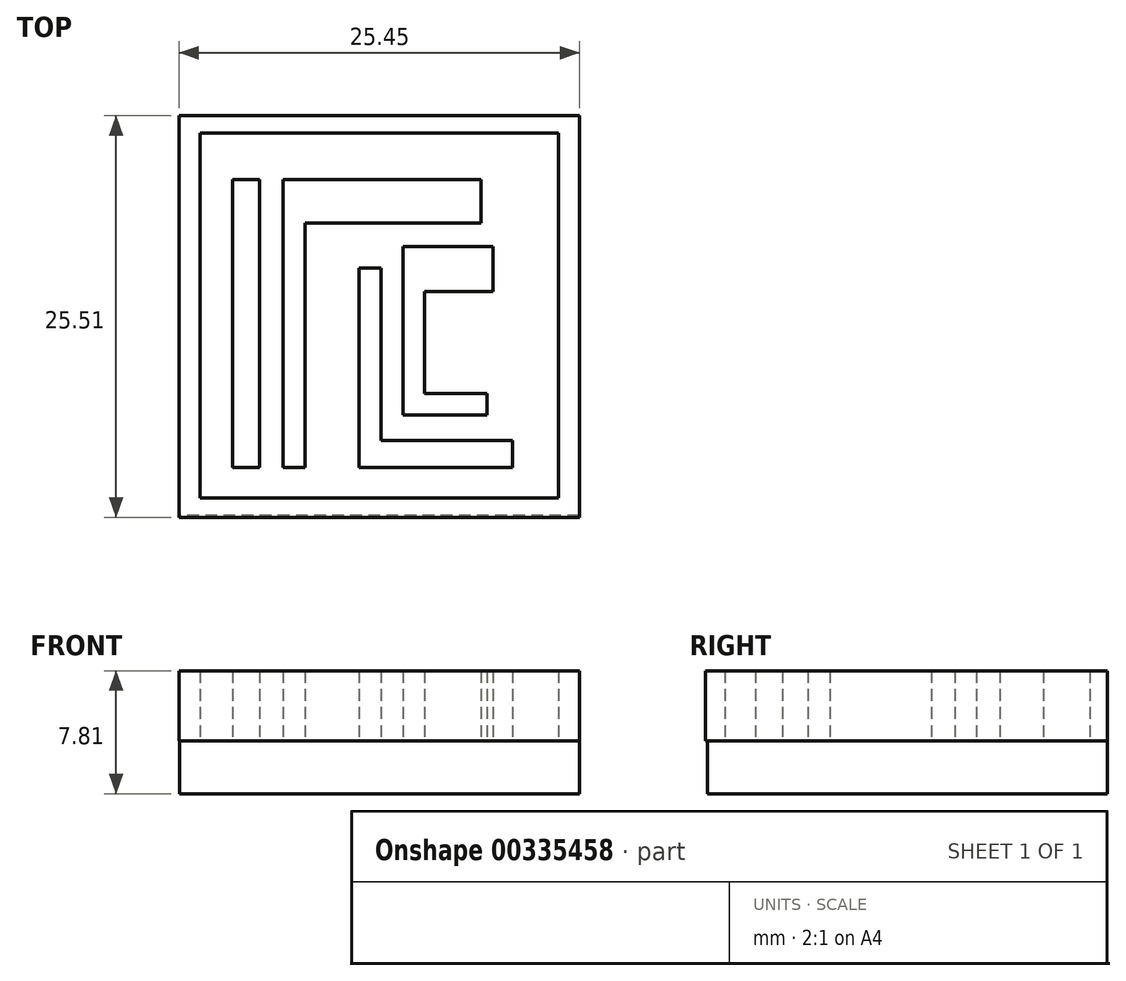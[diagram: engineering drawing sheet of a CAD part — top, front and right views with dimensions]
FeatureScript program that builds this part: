
annotation { "Feature Type Name" : "Feature", "Feature Type Description" : "" }
export const myFeature = defineFeature(function(context is Context, id is Id, definition is map)
    precondition{}
    {
        {
            var Q0;
            Q0=qCreatedBy(makeId("Front.planeOp"),FACE);
            var sketch = newSketch(context, id + "F0", { "sketchPlane" : qUnion([Q0])});
            skLineSegment(sketch, "E0", {"start": v(-11.4, 0) * mm, "end": v(14, 0) * mm});
            skLineSegment(sketch, "E1", {"start": v(14, 0) * mm, "end": v(14, -3.36) * mm});
            skLineSegment(sketch, "E2", {"start": v(14, -3.36) * mm, "end": v(-11.4, -3.36) * mm});
            skLineSegment(sketch, "E3", {"start": v(-11.4, -3.36) * mm, "end": v(-11.4, 0) * mm});
            skSolve(sketch);
        }
        {
            var Q0;
            Q0=makeQuery(id+"F0.imprint","IMPRINT",FACE,{"disambiguationData":[TD([[makeQuery(id+"F0.imprint","IMPRINT",EDGE,{"derivedFrom":sQuery(id+"F0.wireOp",EDGE,"E0")}),-1.0]])]});
            extrude(context, id + "F1", {"entities" : qUnion([Q0]), "depth" : 25.4 * mm});
        }
        {
            var Q0;
            Q0=qCreatedBy(makeId("Top.planeOp"),FACE);
            var sketch = newSketch(context, id + "F2", { "sketchPlane" : qUnion([Q0])});
            skLineSegment(sketch, "E4", {"start": v(-11.43, 0) * mm, "end": v(-11.43, -25.51) * mm});
            skLineSegment(sketch, "E5", {"start": v(-11.43, -25.51) * mm, "end": v(14.02, -25.51) * mm});
            skLineSegment(sketch, "E6", {"start": v(14.02, -25.51) * mm, "end": v(14.02, 0) * mm});
            skLineSegment(sketch, "E7", {"start": v(14.02, 0) * mm, "end": v(-11.43, 0) * mm});
            skLineSegment(sketch, "E8", {"start": v(-11.43, 0) * mm, "end": v(-10.1, -1.11) * mm});
            skLineSegment(sketch, "E9", {"start": v(-11.43, -25.51) * mm, "end": v(-10.1, -24.28) * mm});
            skLineSegment(sketch, "E10", {"start": v(-10.1, -24.28) * mm, "end": v(-10.1, -1.11) * mm});
            skLineSegment(sketch, "E11", {"start": v(14.02, 0) * mm, "end": v(12.69, -1.11) * mm});
            skLineSegment(sketch, "E12", {"start": v(12.69, -1.11) * mm, "end": v(12.69, -24.28) * mm});
            skLineSegment(sketch, "E13", {"start": v(12.69, -24.28) * mm, "end": v(14.02, -25.51) * mm});
            skLineSegment(sketch, "E14", {"start": v(12.69, -24.28) * mm, "end": v(-10.1, -24.28) * mm});
            skLineSegment(sketch, "E15", {"start": v(-10.1, -1.11) * mm, "end": v(12.69, -1.11) * mm});
            skSolve(sketch);
        }
        {
            var Q0;
            Q0=makeQuery(id+"F2.imprint","IMPRINT",FACE,{"disambiguationData":[TD([[makeQuery(id+"F2.imprint","IMPRINT",EDGE,{"derivedFrom":sQuery(id+"F2.wireOp",EDGE,"E4")}),1.0]])]});
            var Q1;
            Q1=makeQuery(id+"F2.imprint","IMPRINT",FACE,{"disambiguationData":[TD([[makeQuery(id+"F2.imprint","IMPRINT",EDGE,{"derivedFrom":sQuery(id+"F2.wireOp",EDGE,"E8")}),1.0]])]});
            var Q2;
            Q2=makeQuery(id+"F2.imprint","IMPRINT",FACE,{"disambiguationData":[TD([[makeQuery(id+"F2.imprint","IMPRINT",EDGE,{"derivedFrom":sQuery(id+"F2.wireOp",EDGE,"E6")}),1.0]])]});
            var Q3;
            Q3=makeQuery(id+"F2.imprint","IMPRINT",FACE,{"disambiguationData":[TD([[makeQuery(id+"F2.imprint","IMPRINT",EDGE,{"derivedFrom":sQuery(id+"F2.wireOp",EDGE,"E5")}),1.0]])]});
            extrude(context, id + "F3", {"entities" : qUnion([Q0, Q1, Q2, Q3]), "operationType" : NewBodyOperationType.ADD, "depth" : 4.44 * mm});
        }
        {
            var Q0;
            Q0=qCreatedBy(makeId("Top.planeOp"),FACE);
            var sketch = newSketch(context, id + "F4", { "sketchPlane" : qUnion([Q0])});
            skLineSegment(sketch, "E16", {"start": v(-8.04, -22.36) * mm, "end": v(-8.04, -4.07) * mm});
            skLineSegment(sketch, "E17", {"start": v(-8.04, -4.07) * mm, "end": v(-6.3, -4.07) * mm});
            skLineSegment(sketch, "E18", {"start": v(-6.3, -4.07) * mm, "end": v(-6.3, -22.36) * mm});
            skLineSegment(sketch, "E19", {"start": v(-6.3, -22.36) * mm, "end": v(-8.04, -22.36) * mm});
            skLineSegment(sketch, "E20", {"start": v(0, -4.07) * mm, "end": v(7.77, -4.07) * mm});
            skLineSegment(sketch, "E21", {"start": v(7.77, -4.07) * mm, "end": v(7.77, -6.8) * mm});
            skLineSegment(sketch, "E22", {"start": v(7.77, -6.8) * mm, "end": v(-3.43, -6.8) * mm});
            skLineSegment(sketch, "E23", {"start": v(-3.43, -6.8) * mm, "end": v(-3.43, -22.36) * mm});
            skLineSegment(sketch, "E24", {"start": v(-3.43, -22.36) * mm, "end": v(-4.8, -22.36) * mm});
            skLineSegment(sketch, "E25", {"start": v(-4.8, -22.36) * mm, "end": v(-4.8, -4.07) * mm});
            skLineSegment(sketch, "E26", {"start": v(-4.8, -4.07) * mm, "end": v(0, -4.07) * mm});
            skLineSegment(sketch, "E27", {"start": v(0, -9.66) * mm, "end": v(0, -22.36) * mm});
            skLineSegment(sketch, "E28", {"start": v(0, -22.36) * mm, "end": v(9.76, -22.36) * mm});
            skLineSegment(sketch, "E29", {"start": v(9.76, -22.36) * mm, "end": v(9.76, -20.62) * mm});
            skLineSegment(sketch, "E30", {"start": v(9.76, -20.62) * mm, "end": v(1.42, -20.62) * mm});
            skLineSegment(sketch, "E31", {"start": v(1.42, -20.62) * mm, "end": v(1.42, -9.66) * mm});
            skLineSegment(sketch, "E32", {"start": v(1.42, -9.66) * mm, "end": v(0, -9.66) * mm});
            skLineSegment(sketch, "E33", {"start": v(8.51, -8.3) * mm, "end": v(8.51, -11.16) * mm});
            skLineSegment(sketch, "E34", {"start": v(8.51, -11.16) * mm, "end": v(4.16, -11.16) * mm});
            skLineSegment(sketch, "E35", {"start": v(4.16, -11.16) * mm, "end": v(4.16, -17.63) * mm});
            skLineSegment(sketch, "E36", {"start": v(4.16, -17.63) * mm, "end": v(8.14, -17.63) * mm});
            skLineSegment(sketch, "E37", {"start": v(8.14, -17.63) * mm, "end": v(8.14, -19) * mm});
            skLineSegment(sketch, "E38", {"start": v(8.14, -19) * mm, "end": v(2.79, -19) * mm});
            skLineSegment(sketch, "E39", {"start": v(2.79, -19) * mm, "end": v(2.79, -8.3) * mm});
            skLineSegment(sketch, "E40", {"start": v(2.79, -8.3) * mm, "end": v(8.51, -8.3) * mm});
            skSolve(sketch);
        }
        {
            var Q0;
            Q0=makeQuery(id+"F4.imprint","IMPRINT",FACE,{"disambiguationData":[TD([[makeQuery(id+"F4.imprint","IMPRINT",EDGE,{"derivedFrom":sQuery(id+"F4.wireOp",EDGE,"E16")}),-1.0]])]});
            var Q1;
            Q1=makeQuery(id+"F4.imprint","IMPRINT",FACE,{"disambiguationData":[TD([[makeQuery(id+"F4.imprint","IMPRINT",EDGE,{"derivedFrom":sQuery(id+"F4.wireOp",EDGE,"E20")}),-1.0]])]});
            var Q2;
            Q2=makeQuery(id+"F4.imprint","IMPRINT",FACE,{"disambiguationData":[TD([[makeQuery(id+"F4.imprint","IMPRINT",EDGE,{"derivedFrom":sQuery(id+"F4.wireOp",EDGE,"E27")}),1.0]])]});
            var Q3;
            Q3=makeQuery(id+"F4.imprint","IMPRINT",FACE,{"disambiguationData":[TD([[makeQuery(id+"F4.imprint","IMPRINT",EDGE,{"derivedFrom":sQuery(id+"F4.wireOp",EDGE,"E33")}),-1.0]])]});
            extrude(context, id + "F5", {"entities" : qUnion([Q0, Q1, Q2, Q3]), "operationType" : NewBodyOperationType.ADD, "depth" : 4.44 * mm});
        }
    });
